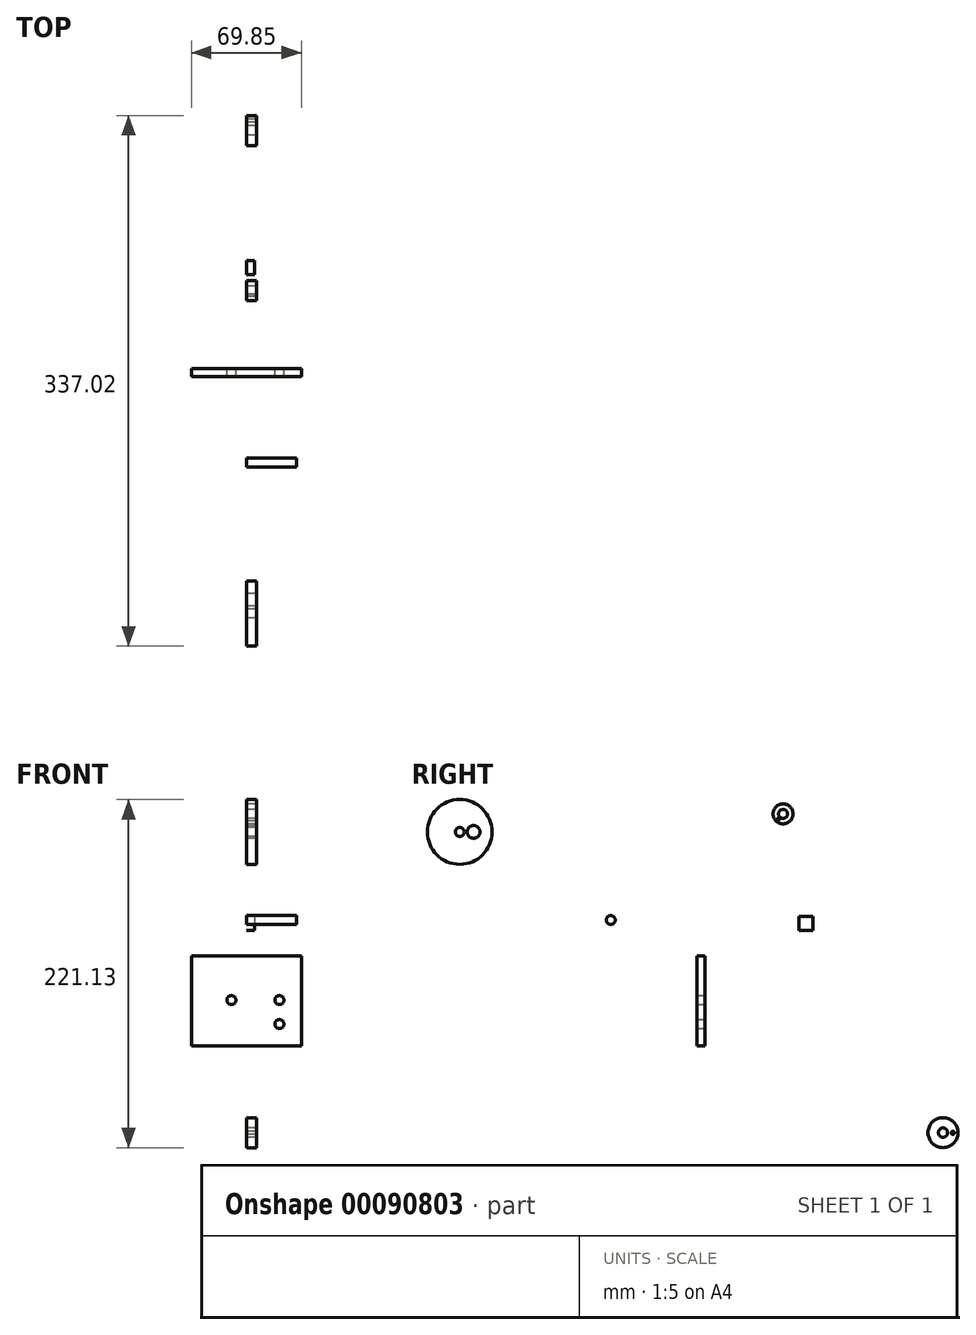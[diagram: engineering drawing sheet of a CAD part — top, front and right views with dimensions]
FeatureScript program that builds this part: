
annotation { "Feature Type Name" : "Feature", "Feature Type Description" : "" }
export const myFeature = defineFeature(function(context is Context, id is Id, definition is map)
    precondition{}
    {
        {
            var Q0;
            Q0=qCreatedBy(makeId("Front.planeOp"),FACE);
            var sketch = newSketch(context, id + "F0", { "sketchPlane" : qUnion([Q0])});
            skLineSegment(sketch, "E0.bottom", {"start": v(-34.92, 32.77) * mm, "end": v(34.93, 32.77) * mm});
            skLineSegment(sketch, "E0.top", {"start": v(-34.92, -24.38) * mm, "end": v(34.93, -24.38) * mm});
            skLineSegment(sketch, "E0.left", {"start": v(-34.92, 32.77) * mm, "end": v(-34.92, -24.38) * mm});
            skLineSegment(sketch, "E0.right", {"start": v(34.93, 32.77) * mm, "end": v(34.93, -24.38) * mm});
            skLineSegment(sketch, "E1", {"start": v(-34.92, 4.83) * mm, "end": v(34.93, 4.83) * mm, "construction": true});
            skLineSegment(sketch, "E2", {"start": v(-9.52, 32.77) * mm, "end": v(-9.52, -24.38) * mm, "construction": true});
            skLineSegment(sketch, "E3", {"start": v(20.96, 32.77) * mm, "end": v(20.96, -24.38) * mm, "construction": true});
            skLineSegment(sketch, "E4", {"start": v(-34.92, -10.41) * mm, "end": v(34.93, -10.41) * mm, "construction": true});
            skCircle(sketch, "E5", {"center": v(-9.52, 4.83) * mm, "radius": 2.86 * mm});
            skCircle(sketch, "E6", {"center": v(20.96, 4.83) * mm, "radius": 2.86 * mm});
            skCircle(sketch, "E7", {"center": v(20.96, -10.41) * mm, "radius": 2.86 * mm});
            skSolve(sketch);
        }
        {
            var Q0;
            Q0=makeQuery(id+"F0.imprint","IMPRINT",FACE,{"disambiguationData":[TD([[makeQuery(id+"F0.imprint","IMPRINT",EDGE,{"derivedFrom":sQuery(id+"F0.wireOp",EDGE,"E0.bottom")}),-1.0]])]});
            extrude(context, id + "F1", {"entities" : qUnion([Q0]), "depth" : 5.08 * mm});
        }
        {
            var Q0;
            Q0=qCreatedBy(makeId("Right.planeOp"),FACE);
            var sketch = newSketch(context, id + "F2", { "sketchPlane" : qUnion([Q0])});
            skCircle(sketch, "E8", {"center": v(-155.75, 111.66) * mm, "radius": 20.57 * mm});
            skCircle(sketch, "E9", {"center": v(49.58, 123.1) * mm, "radius": 6.35 * mm});
            skCircle(sketch, "E10", {"center": v(151.18, -79.36) * mm, "radius": 9.53 * mm});
            skCircle(sketch, "E11", {"center": v(-155.75, 111.66) * mm, "radius": 2.86 * mm});
            skCircle(sketch, "E12", {"center": v(151.18, -79.36) * mm, "radius": 2.95 * mm});
            skCircle(sketch, "E13", {"center": v(49.58, 123.1) * mm, "radius": 2.86 * mm});
            skCircle(sketch, "E14", {"center": v(-146.98, 111.66) * mm, "radius": 4.06 * mm});
            skCircle(sketch, "E15", {"center": v(157.4, -79.45) * mm, "radius": 1.03 * mm});
            skCircle(sketch, "E16", {"center": v(46.36, 119.47) * mm, "radius": 0.82 * mm});
            skSolve(sketch);
        }
        {
            var Q0;
            Q0 = qSketchRegion(id + "F2", true);
            extrude(context, id + "F3", {"entities" : qUnion([Q0]), "depth" : 6.35 * mm});
        }
        {
            var Q0;
            Q0=qCreatedBy(makeId("Right.planeOp"),FACE);
            var sketch = newSketch(context, id + "F4", { "sketchPlane" : qUnion([Q0])});
            skCircle(sketch, "E17", {"center": v(-59.85, 55.71) * mm, "radius": 2.86 * mm});
            skSolve(sketch);
        }
        {
            var Q0;
            Q0 = qSketchRegion(id + "F4", true);
            extrude(context, id + "F5", {"entities" : qUnion([Q0]), "depth" : 31.75 * mm});
        }
        {
            var Q0;
            Q0=qCreatedBy(makeId("Right.planeOp"),FACE);
            var sketch = newSketch(context, id + "F6", { "sketchPlane" : qUnion([Q0])});
            skLineSegment(sketch, "E18.bottom", {"start": v(68.47, 58.1) * mm, "end": v(59.58, 58.1) * mm});
            skLineSegment(sketch, "E18.top", {"start": v(68.47, 49.21) * mm, "end": v(59.58, 49.21) * mm});
            skLineSegment(sketch, "E18.left", {"start": v(68.47, 58.1) * mm, "end": v(68.47, 49.21) * mm});
            skLineSegment(sketch, "E18.right", {"start": v(59.58, 58.1) * mm, "end": v(59.58, 49.21) * mm});
            skSolve(sketch);
        }
        {
            var Q0;
            Q0=makeQuery(id+"F6.imprint","IMPRINT",FACE,{"disambiguationData":[TD([[makeQuery(id+"F6.imprint","IMPRINT",EDGE,{"derivedFrom":sQuery(id+"F6.wireOp",EDGE,"E18.bottom")}),1.0]])]});
            extrude(context, id + "F7", {"entities" : qUnion([Q0]), "depth" : 5.08 * mm});
        }
    });
